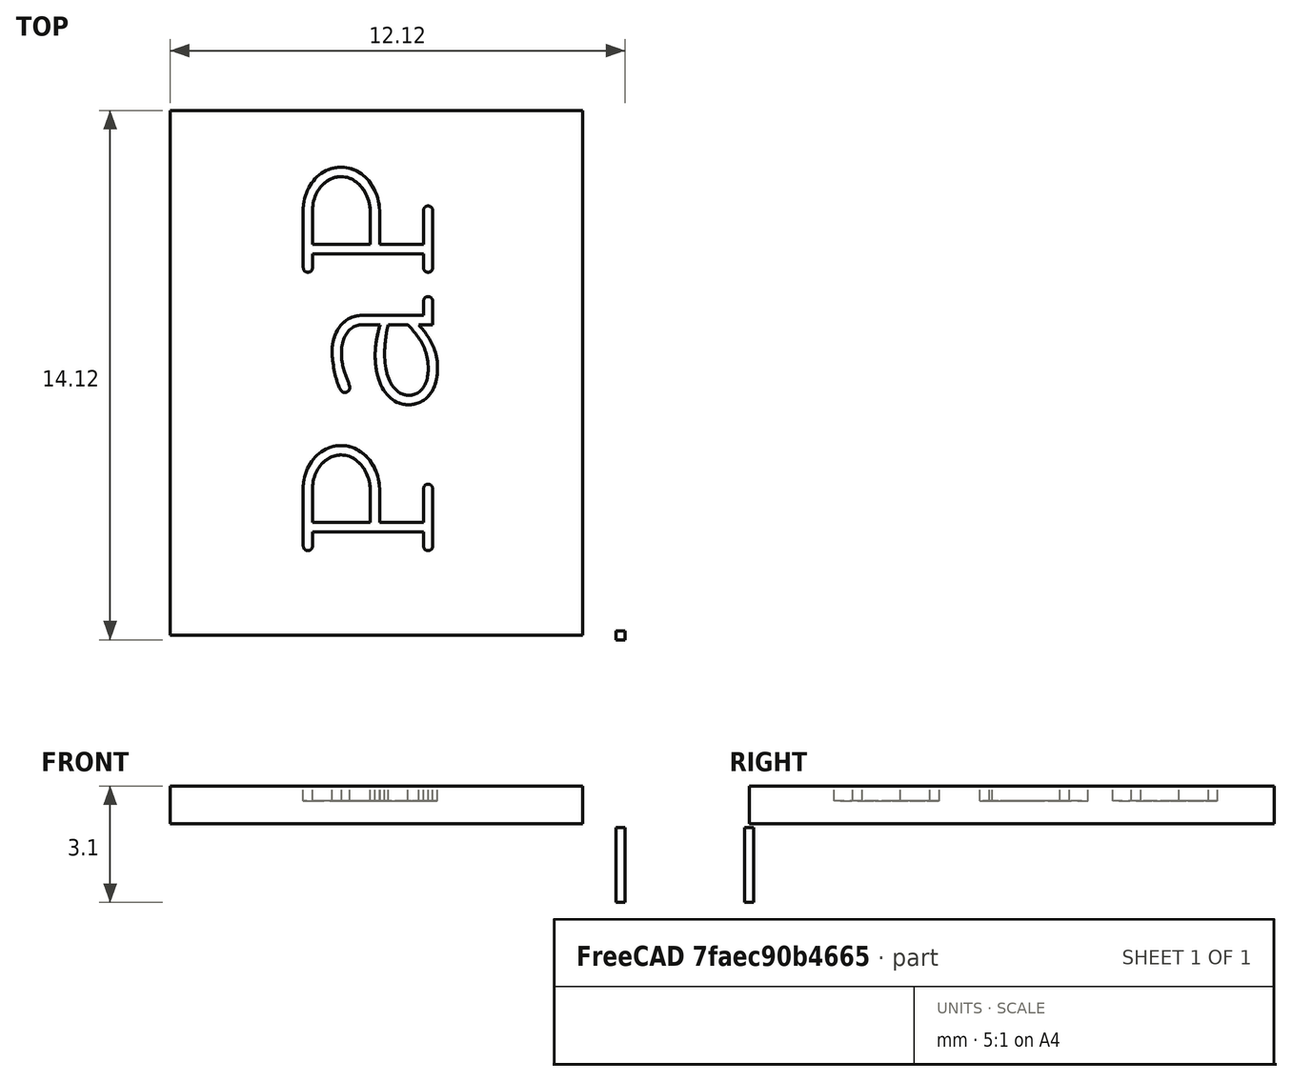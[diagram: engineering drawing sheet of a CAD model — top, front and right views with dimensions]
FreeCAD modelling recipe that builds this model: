
FCSTD DOCUMENT  (FreeCAD 0.16R)
Label: led
License: All rights reserved
LicenseURL: http://en.wikipedia.org/wiki/All_rights_reserved
objects: App::VRMLObject×2, Part::Box×2, Part::FeaturePython×1, Part::Part2DObjectPython×1, PartDesign::Pad×1, Part::Cut×1
note: 7 computed .brp shape members not serialized (recipe doc carries the construction recipe); baked Part::Feature solids carry a one-line shape summary decoded from their .brp

FEATURE [App::VRMLObject] led5_rect
FEATURE [Part::Box] Box  label="Cube"
  Height = 2
  Length = 0.24
  Placement = pos=(-0.12,-0.12,-2.7) rot=(0,0,1;0rad)
  Width = 0.24
FEATURE [Part::FeaturePython] Clone  label="Clone of Cube"  # Draft clone (typed FeaturePython)
  Objects = -> [Box]
  Placement = pos=(0.88,-0.12,-2.7) rot=(0,0,1;0rad)
  Scale = (1,1,1)
FEATURE [App::VRMLObject] led5p_
FEATURE [Part::Box] Box001  label="Cube001"
  Height = 1
  Length = 14
  Placement = pos=(0,0,-0.6) rot=(0,0,1;0rad)
  Width = 11
FEATURE [Part::Part2DObjectPython] ShapeString  # Draft 2D object (typed FeaturePython)
  FontFile = <path>
  Placement = pos=(2,4,0) rot=(0,0,1;0rad)
  Size = 2
  String = PaP
  Tracking = 0
FEATURE [PartDesign::Pad] Pad
  Length = 0.5
  Length2 = 100
  Placement = pos=(2,4,0) rot=(0,0,1;0rad)
  Sketch = -> ShapeString
  Type = 0
FEATURE [Part::Cut] Cut
  Base = -> Box001
  Placement = pos=(0,0,0) rot=(0,0,1;1.5708rad)
  Tool = -> Pad
note: 1 file-system path scrubbed to <path> (originals preserved in the JSON sidecar)
